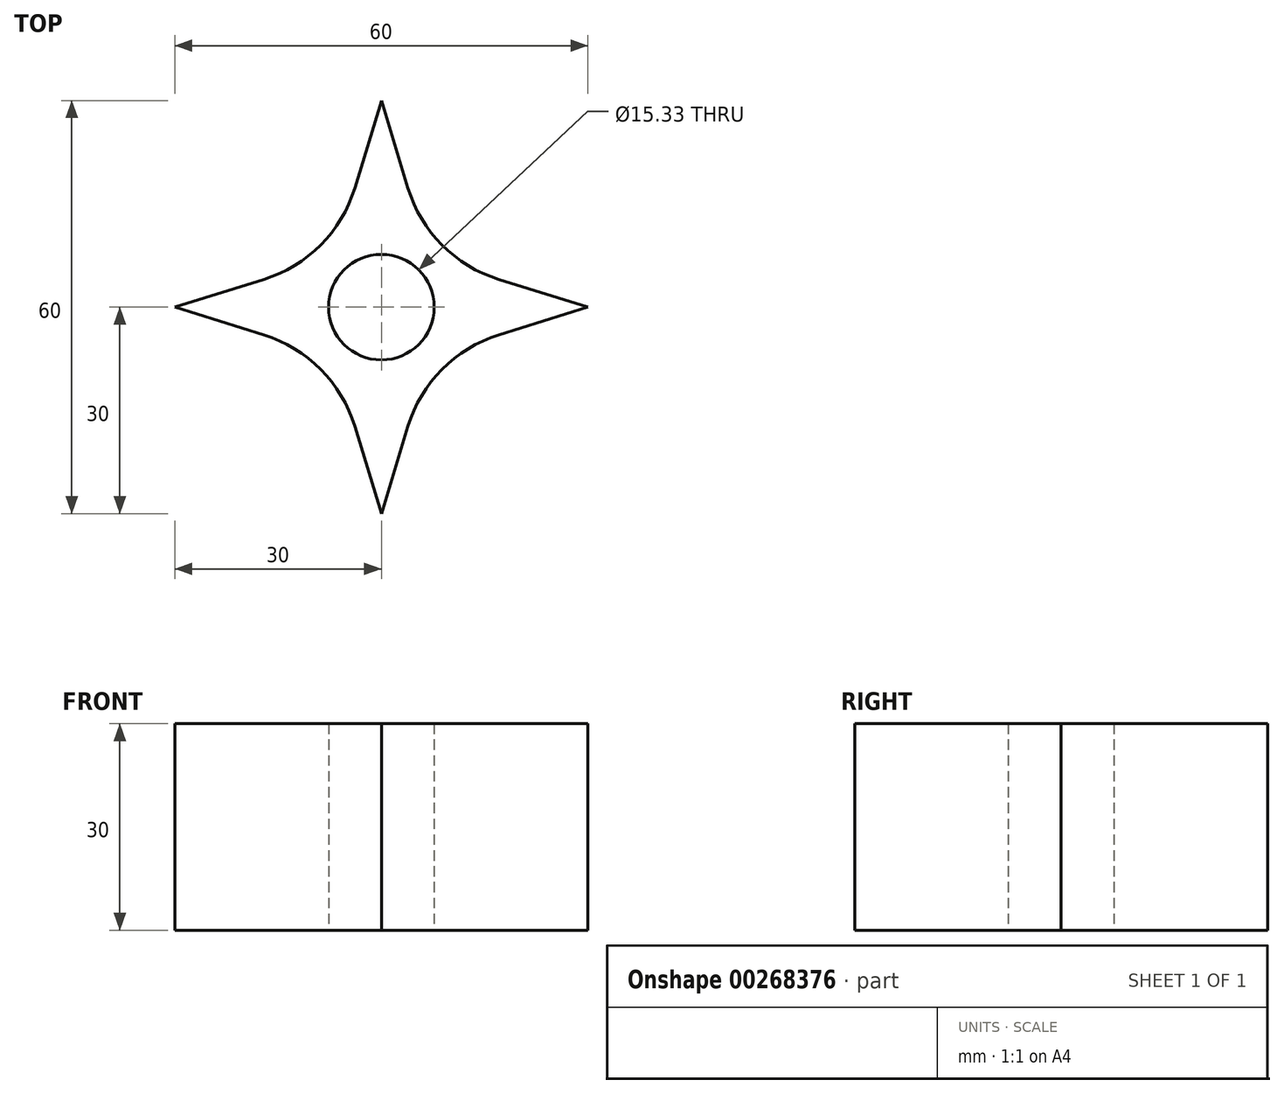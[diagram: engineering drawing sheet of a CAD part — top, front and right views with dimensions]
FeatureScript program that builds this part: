
annotation { "Feature Type Name" : "Feature", "Feature Type Description" : "" }
export const myFeature = defineFeature(function(context is Context, id is Id, definition is map)
    precondition{}
    {
        {
            var Q0;
            Q0=qCreatedBy(makeId("Top.planeOp"),FACE);
            var sketch = newSketch(context, id + "F0", { "sketchPlane" : qUnion([Q0])});
            skLineSegment(sketch, "E0", {"start": v(6.95, 7.19) * mm, "end": v(30, 0) * mm});
            skLineSegment(sketch, "E1", {"start": v(6.95, 7.19) * mm, "end": v(0, 30) * mm});
            skLineSegment(sketch, "E2.MirrorCS", {"start": v(-6.95, 7.19) * mm, "end": v(-30, 0) * mm});
            skLineSegment(sketch, "E3.MirrorCS", {"start": v(-6.95, 7.19) * mm, "end": v(0, 30) * mm});
            skLineSegment(sketch, "E4.MirrorCS", {"start": v(-6.95, -7.19) * mm, "end": v(-30, 0) * mm});
            skLineSegment(sketch, "E5.MirrorCS", {"start": v(-6.95, -7.19) * mm, "end": v(0, -30) * mm});
            skLineSegment(sketch, "E6.MirrorCS", {"start": v(6.95, -7.19) * mm, "end": v(0, -30) * mm});
            skLineSegment(sketch, "E7.MirrorCS", {"start": v(6.95, -7.19) * mm, "end": v(30, 0) * mm});
            skCircle(sketch, "E8", {"center": v(0, 0) * mm, "radius": 7.66 * mm});
            skSolve(sketch);
        }
        {
            var Q0;
            Q0=makeQuery(id+"F0.imprint","IMPRINT",FACE,{"disambiguationData":[TD([[makeQuery(id+"F0.imprint","IMPRINT",EDGE,{"derivedFrom":sQuery(id+"F0.wireOp",EDGE,"E0")}),-1.0]])]});
            extrude(context, id + "F1", {"entities" : qUnion([Q0]), "depth" : 30 * mm});
        }
        {
            var Q0;
            Q0=makeQuery(id+"F1.opExtrude","SWEPT_EDGE",EDGE,{"disambiguationData":[OSD([sQuery(id+"F0.wireOp",EDGE,"E4.MirrorCS"),sQuery(id+"F0.wireOp",EDGE,"E5.MirrorCS")])]});
            var Q1;
            Q1=makeQuery(id+"F1.opExtrude","SWEPT_EDGE",EDGE,{"disambiguationData":[OSD([sQuery(id+"F0.wireOp",EDGE,"E6.MirrorCS"),sQuery(id+"F0.wireOp",EDGE,"E7.MirrorCS")])]});
            var Q2;
            Q2=makeQuery(id+"F1.opExtrude","SWEPT_EDGE",EDGE,{"disambiguationData":[OSD([sQuery(id+"F0.wireOp",EDGE,"E0"),sQuery(id+"F0.wireOp",EDGE,"E1")])]});
            var Q3;
            Q3=makeQuery(id+"F1.opExtrude","SWEPT_EDGE",EDGE,{"disambiguationData":[OSD([sQuery(id+"F0.wireOp",EDGE,"E2.MirrorCS"),sQuery(id+"F0.wireOp",EDGE,"E3.MirrorCS")])]});
            fillet(context, id + "F2", {"entities" : qUnion([Q0, Q1, Q2, Q3]), "radius" : 20 * mm, "tangentPropagation" : true, "allowEdgeOverflow" : false});
        }
    });
